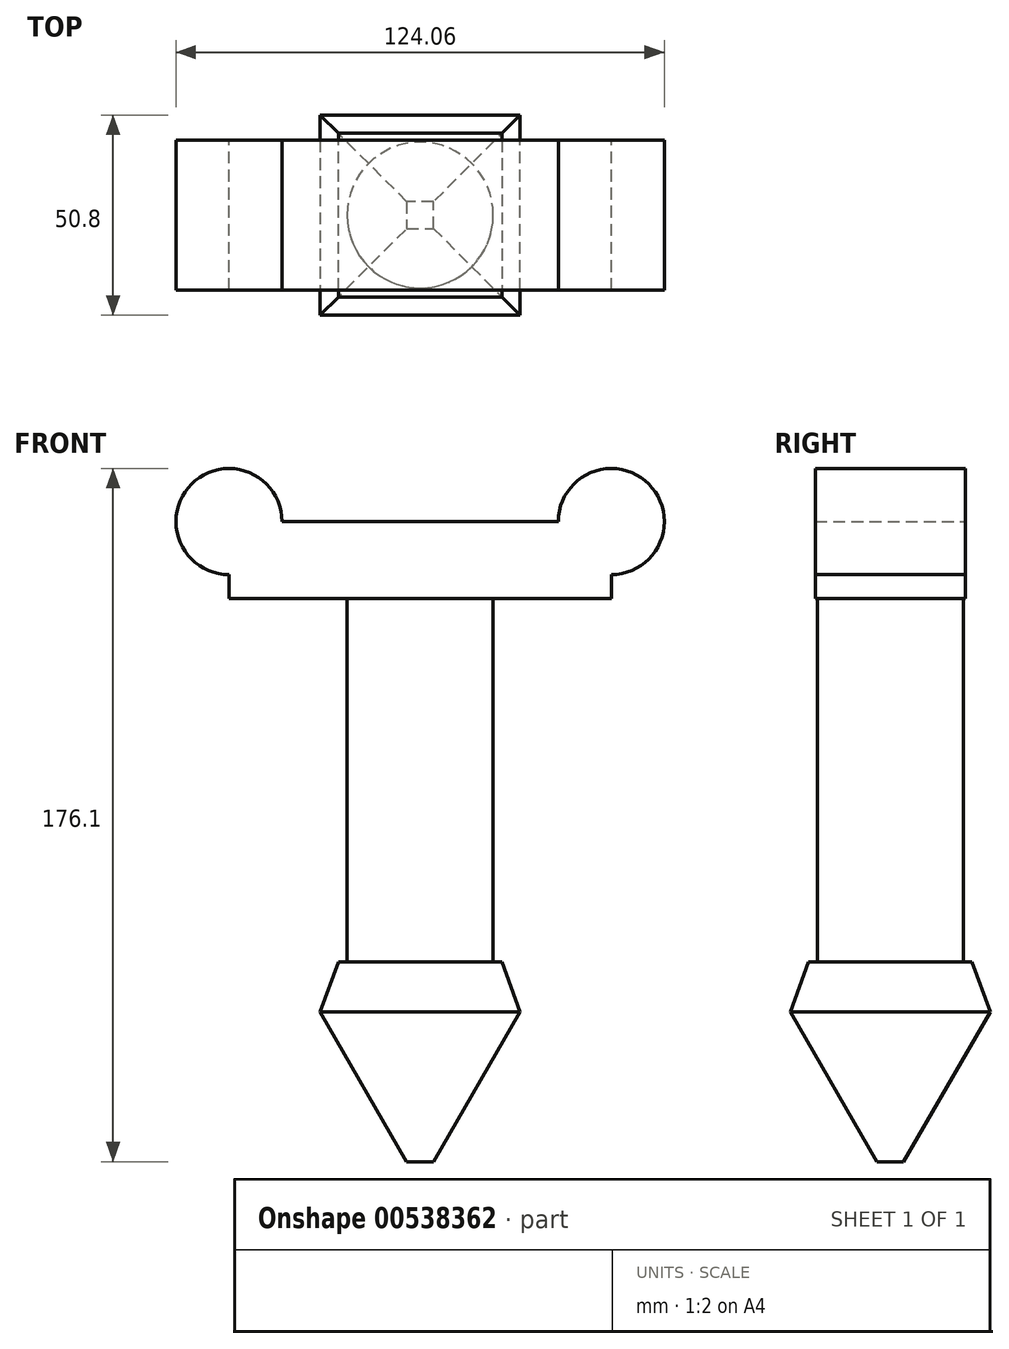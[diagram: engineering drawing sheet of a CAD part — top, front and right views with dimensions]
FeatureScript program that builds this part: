
annotation { "Feature Type Name" : "Feature", "Feature Type Description" : "" }
export const myFeature = defineFeature(function(context is Context, id is Id, definition is map)
    precondition{}
    {
        {
            var Q0;
            Q0=qCreatedBy(makeId("Top.planeOp"),FACE);
            var sketch = newSketch(context, id + "F0", { "sketchPlane" : qUnion([Q0])});
            skLineSegment(sketch, "E0.bottom", {"start": v(25.4, 25.4) * mm, "end": v(-25.4, 25.4) * mm});
            skLineSegment(sketch, "E0.top", {"start": v(25.4, -25.4) * mm, "end": v(-25.4, -25.4) * mm});
            skLineSegment(sketch, "E0.left", {"start": v(25.4, 25.4) * mm, "end": v(25.4, -25.4) * mm});
            skLineSegment(sketch, "E0.right", {"start": v(-25.4, 25.4) * mm, "end": v(-25.4, -25.4) * mm});
            skPoint(sketch, "E0.middle", {"position": v(0, 0) * mm});
            skSolve(sketch);
        }
        {
            var Q0;
            Q0 = qSketchRegion(id + "F0", true);
            extrude(context, id + "F1", {"entities" : qUnion([Q0]), "oppositeDirection" : true, "depth" : 38.1 * mm, "offsetDistance" : 25.4 * mm, "hasDraft" : true, "draftAngle" : 30 * degree, "draftPullDirection" : true});
        }
        {
            var Q0;
            Q0=makeQuery(id+"F1.opExtrude","CAP_FACE",FACE,{"disambiguationData":[OSD([sQuery(id+"F0.wireOp",EDGE,"E0.bottom"),sQuery(id+"F0.wireOp",EDGE,"E0.top"),sQuery(id+"F0.wireOp",EDGE,"E0.left"),sQuery(id+"F0.wireOp",EDGE,"E0.right")])],"isStart":true});
            extrude(context, id + "F2", {"entities" : qUnion([Q0]), "operationType" : NewBodyOperationType.ADD, "depth" : 12.7 * mm, "offsetDistance" : 25.4 * mm, "hasDraft" : true, "draftAngle" : 20 * degree, "draftPullDirection" : true});
        }
        {
            var Q0;
            Q0=makeQuery(id+"F2.opExtrude","CAP_FACE",FACE,{"disambiguationData":[OSD([sQuery(id+"F0.wireOp",EDGE,"E0.bottom"),sQuery(id+"F0.wireOp",EDGE,"E0.top"),sQuery(id+"F0.wireOp",EDGE,"E0.left"),sQuery(id+"F0.wireOp",EDGE,"E0.right")])],"isStart":false});
            var sketch = newSketch(context, id + "F3", { "sketchPlane" : qUnion([Q0])});
            skCircle(sketch, "E1", {"center": v(0, 0) * mm, "radius": 18.54 * mm});
            skSolve(sketch);
        }
        {
            var Q0;
            Q0 = qSketchRegion(id + "F3", true);
            extrude(context, id + "F4", {"entities" : qUnion([Q0]), "operationType" : NewBodyOperationType.ADD, "depth" : 101.6 * mm, "offsetDistance" : 25.4 * mm});
        }
        {
            var Q0;
            Q0=qCreatedBy(makeId("Front.planeOp"),FACE);
            var sketch = newSketch(context, id + "F5", { "sketchPlane" : qUnion([Q0])});
            skLineSegment(sketch, "E2.bottom", {"start": v(35.08, 124.53) * mm, "end": v(-35.08, 124.53) * mm});
            skLineSegment(sketch, "E2.top", {"start": v(48.56, 105.02) * mm, "end": v(-48.56, 105.02) * mm});
            skLineSegment(sketch, "E2.left", {"start": v(48.56, 111.05) * mm, "end": v(48.56, 105.02) * mm});
            skLineSegment(sketch, "E2.right", {"start": v(-48.56, 111.05) * mm, "end": v(-48.56, 105.02) * mm});
            skPoint(sketch, "E2.middle", {"position": v(0, 114.77) * mm});
            skArc(sketch, "E3", {"start": v(-35.08, 124.53) * mm, "mid": v(-58.09, 134.05) * mm, "end": v(-48.56, 111.05) * mm});
            skArc(sketch, "E4", {"start": v(48.56, 111.05) * mm, "mid": v(58.09, 134.05) * mm, "end": v(35.08, 124.53) * mm});
            skSolve(sketch);
        }
        {
            var Q0;
            Q0 = qSketchRegion(id + "F5", true);
            extrude(context, id + "F6", {"entities" : qUnion([Q0]), "operationType" : NewBodyOperationType.ADD, "endBound" : BoundingType.SYMMETRIC, "depth" : 38.1 * mm, "offsetDistance" : 25.4 * mm});
        }
    });
